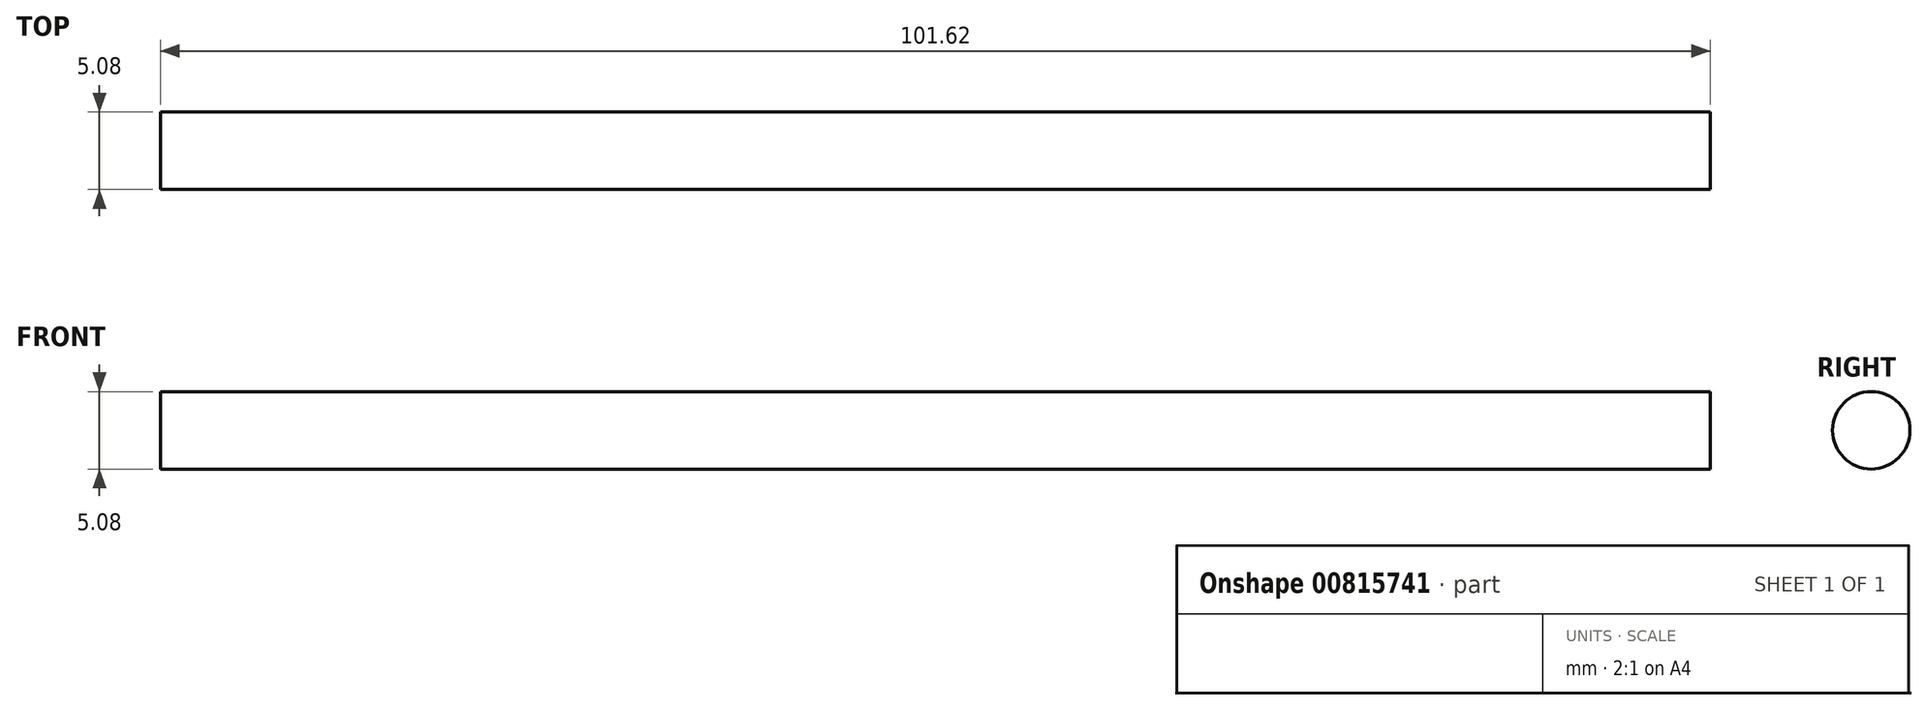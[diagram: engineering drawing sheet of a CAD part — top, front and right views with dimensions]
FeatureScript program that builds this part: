
annotation { "Feature Type Name" : "Feature", "Feature Type Description" : "" }
export const myFeature = defineFeature(function(context is Context, id is Id, definition is map)
    precondition{}
    {
        {
            var Q0;
            Q0=qCreatedBy(makeId("Top.planeOp"),FACE);
            var sketch = newSketch(context, id + "F0", { "sketchPlane" : qUnion([Q0])});
            skLineSegment(sketch, "E0", {"start": v(-30.21, 0) * mm, "end": v(71.39, 0) * mm});
            skLineSegment(sketch, "E1", {"start": v(-30.23, 2.54) * mm, "end": v(71.37, 2.54) * mm});
            skLineSegment(sketch, "E2", {"start": v(-30.23, 2.54) * mm, "end": v(-30.21, 0) * mm});
            skLineSegment(sketch, "E3", {"start": v(71.37, 2.54) * mm, "end": v(71.39, 0) * mm});
            skLineSegment(sketch, "E4", {"start": v(-30.23, 33.4) * mm, "end": v(-30.23, -37.88) * mm});
            skLineSegment(sketch, "E5", {"start": v(-49.18, 0) * mm, "end": v(57.3, 0) * mm});
            skSolve(sketch);
        }
        {
            var Q0;
            Q0=makeQuery(id+"F0.imprint","IMPRINT",FACE,{"disambiguationData":[TD([[makeQuery(id+"F0.imprint","IMPRINT",EDGE,{"derivedFrom":sQuery(id+"F0.wireOp",EDGE,"E1")}),-1.0]])]});
            var Q1;
            Q1=sQuery(id+"F0.wireOp",EDGE,"E5");
            revolve(context, id + "F1", {"surfaceOperationType" : NewSurfaceOperationType.NEW, "entities" : qUnion([Q0]), "axis" : qUnion([Q1]), "revolveType" : RevolveType.FULL});
        }
    });
